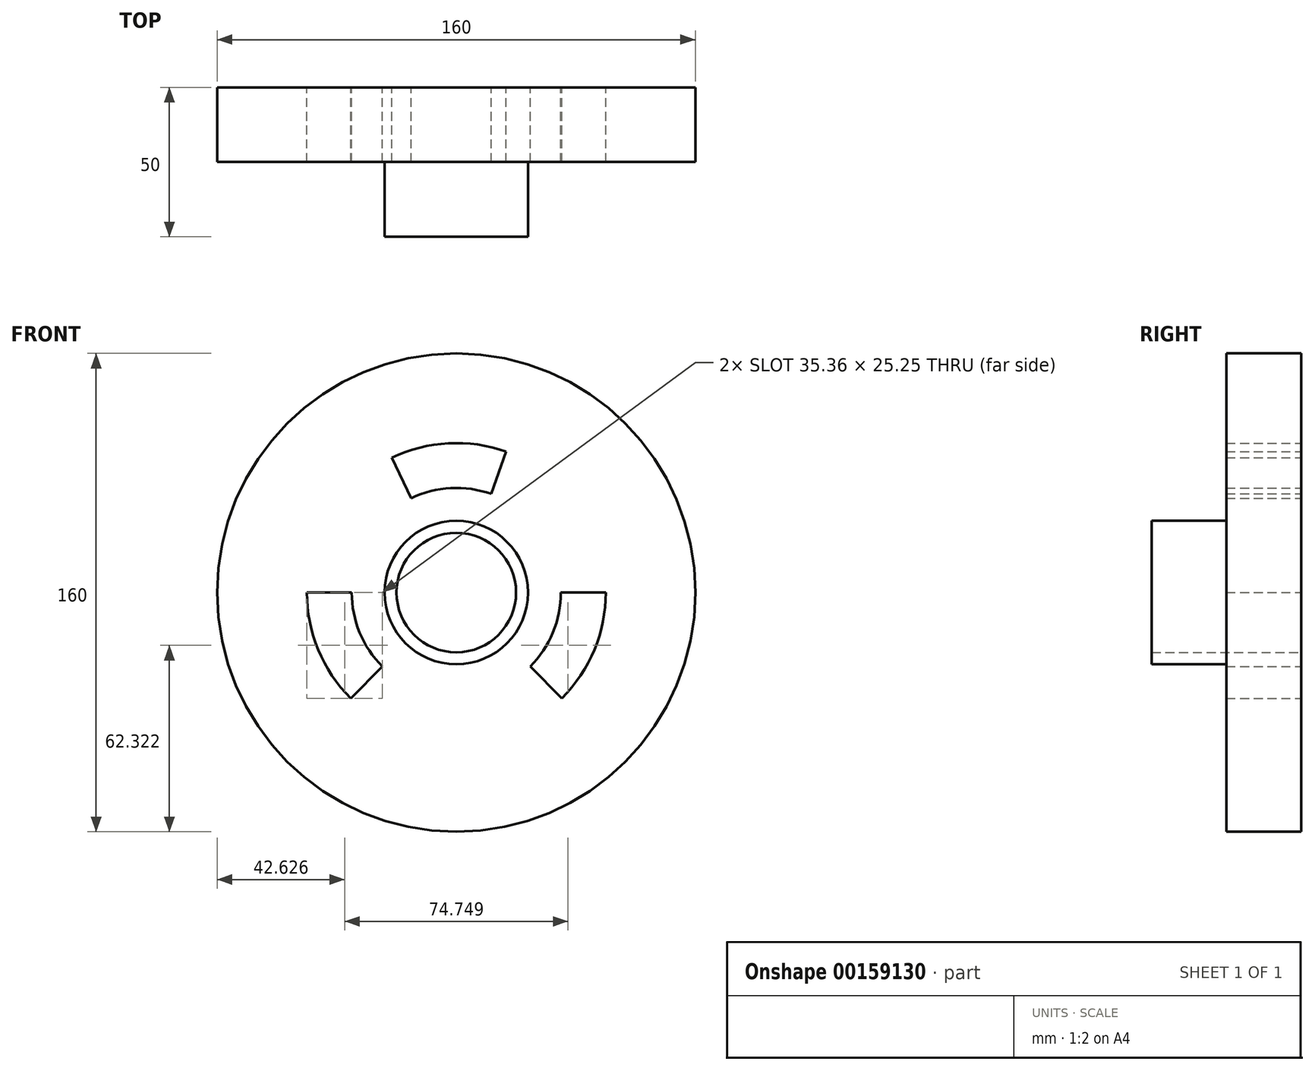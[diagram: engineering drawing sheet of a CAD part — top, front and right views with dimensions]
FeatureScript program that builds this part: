
annotation { "Feature Type Name" : "Feature", "Feature Type Description" : "" }
export const myFeature = defineFeature(function(context is Context, id is Id, definition is map)
    precondition{}
    {
        {
            var Q0;
            Q0=qCreatedBy(makeId("Front.planeOp"),FACE);
            var sketch = newSketch(context, id + "F0", { "sketchPlane" : qUnion([Q0])});
            skCircle(sketch, "E0", {"center": v(0, 0) * mm, "radius": 50 * mm});
            skCircle(sketch, "E1", {"center": v(0, 0) * mm, "radius": 20 * mm});
            skCircle(sketch, "E2", {"center": v(0, 0) * mm, "radius": 80 * mm});
            skLineSegment(sketch, "E3", {"start": v(0, 0) * mm, "end": v(-38.3, 80.1) * mm});
            skLineSegment(sketch, "E4", {"start": v(0, 0) * mm, "end": v(29.56, 83.72) * mm});
            skCircle(sketch, "E5", {"center": v(0, 0) * mm, "radius": 35 * mm});
            skCircle(sketch, "E6", {"center": v(0, 0) * mm, "radius": 24 * mm});
            skLineSegment(sketch, "E7", {"start": v(83.36, 161.24) * mm, "end": v(111.84, 161.24) * mm});
            skArc(sketch, "E8", {"start": v(83.36, 176.24) * mm, "mid": v(68.36, 161.24) * mm, "end": v(83.36, 146.24) * mm});
            skPoint(sketch, "E9", {"position": v(-21.57, 45.1) * mm});
            skPoint(sketch, "E10", {"position": v(-15.1, 31.58) * mm});
            skPoint(sketch, "E11", {"position": v(16.65, 47.15) * mm});
            skPoint(sketch, "E12", {"position": v(11.65, 33) * mm});
            skLineSegment(sketch, "E13", {"start": v(0, 0) * mm, "end": v(109.13, 0) * mm});
            skLineSegment(sketch, "E14", {"start": v(0, 0) * mm, "end": v(-88.87, 0) * mm});
            skLineSegment(sketch, "E15", {"start": v(0, 0) * mm, "end": v(-75.12, -75.12) * mm});
            skLineSegment(sketch, "E16", {"start": v(0, 0) * mm, "end": v(67.75, -67.75) * mm});
            skPoint(sketch, "E17", {"position": v(-50, 0) * mm});
            skPoint(sketch, "E18", {"position": v(-35.36, -35.36) * mm});
            skPoint(sketch, "E19", {"position": v(35.36, -35.36) * mm});
            skPoint(sketch, "E20", {"position": v(50, 0) * mm});
            skSolve(sketch);
        }
        {
            var Q0;
            Q0 = qSketchRegion(id + "F0", true);
            var Q1;
            {var subQ0=sQuery(id+"F0.wireOp",EDGE,"E4");var subQ1=sQuery(id+"F0.wireOp",EDGE,"E0");var subQ2=makeQuery(id+"F0.imprint","INTERSECT",VERTEX,{"derivedFrom":[subQ1,subQ0]});Q1=makeQuery(id+"F0.imprint","IMPRINT",FACE,{"disambiguationData":[TD([[makeQuery(id+"F0.imprint","IMPRINT",EDGE,{"disambiguationData":[TD([[subQ2,1.0]])],"derivedFrom":subQ1}),1.0]])]});}
            var Q2;
            {var subQ0=sQuery(id+"F0.wireOp",EDGE,"E3");var subQ1=sQuery(id+"F0.wireOp",EDGE,"E0");var subQ2=makeQuery(id+"F0.imprint","INTERSECT",VERTEX,{"derivedFrom":[subQ1,subQ0]});Q2=makeQuery(id+"F0.imprint","IMPRINT",FACE,{"disambiguationData":[TD([[makeQuery(id+"F0.imprint","IMPRINT",EDGE,{"disambiguationData":[TD([[subQ2,-1.0]])],"derivedFrom":subQ1}),1.0]])]});}
            var Q3;
            {var subQ0=sQuery(id+"F0.wireOp",EDGE,"E15");var subQ1=sQuery(id+"F0.wireOp",EDGE,"E0");var subQ2=makeQuery(id+"F0.imprint","INTERSECT",VERTEX,{"derivedFrom":[subQ1,subQ0]});Q3=makeQuery(id+"F0.imprint","IMPRINT",FACE,{"disambiguationData":[TD([[makeQuery(id+"F0.imprint","IMPRINT",EDGE,{"disambiguationData":[TD([[subQ2,-1.0]])],"derivedFrom":subQ1}),1.0]])]});}
            var Q4;
            {var subQ0=sQuery(id+"F0.wireOp",EDGE,"E6");var subQ1=sQuery(id+"F0.wireOp",EDGE,"E3");var subQ2=makeQuery(id+"F0.imprint","INTERSECT",VERTEX,{"derivedFrom":[subQ1,subQ0]});Q4=makeQuery(id+"F0.imprint","IMPRINT",FACE,{"disambiguationData":[TD([[makeQuery(id+"F0.imprint","IMPRINT",EDGE,{"disambiguationData":[TD([[subQ2,-1.0]])],"derivedFrom":subQ1}),1.0]])]});}
            var Q5;
            {var subQ0=sQuery(id+"F0.wireOp",EDGE,"E6");var subQ1=sQuery(id+"F0.wireOp",EDGE,"E3");var subQ2=makeQuery(id+"F0.imprint","INTERSECT",VERTEX,{"derivedFrom":[subQ1,subQ0]});Q5=makeQuery(id+"F0.imprint","IMPRINT",FACE,{"disambiguationData":[TD([[makeQuery(id+"F0.imprint","IMPRINT",EDGE,{"disambiguationData":[TD([[subQ2,-1.0]])],"derivedFrom":subQ1}),-1.0]])]});}
            var Q6;
            {var subQ0=sQuery(id+"F0.wireOp",EDGE,"E6");var subQ1=sQuery(id+"F0.wireOp",EDGE,"E4");var subQ2=makeQuery(id+"F0.imprint","INTERSECT",VERTEX,{"derivedFrom":[subQ1,subQ0]});Q6=makeQuery(id+"F0.imprint","IMPRINT",FACE,{"disambiguationData":[TD([[makeQuery(id+"F0.imprint","IMPRINT",EDGE,{"disambiguationData":[TD([[subQ2,-1.0]])],"derivedFrom":subQ1}),-1.0]])]});}
            var Q7;
            {var subQ0=sQuery(id+"F0.wireOp",EDGE,"E13");var subQ1=sQuery(id+"F0.wireOp",EDGE,"E5");var subQ2=makeQuery(id+"F0.imprint","INTERSECT",VERTEX,{"derivedFrom":[subQ1,subQ0]});Q7=makeQuery(id+"F0.imprint","IMPRINT",FACE,{"disambiguationData":[TD([[makeQuery(id+"F0.imprint","IMPRINT",EDGE,{"disambiguationData":[TD([[subQ2,1.0]])],"derivedFrom":subQ1}),1.0]])]});}
            var Q8;
            {var subQ0=sQuery(id+"F0.wireOp",EDGE,"E15");var subQ1=sQuery(id+"F0.wireOp",EDGE,"E5");var subQ2=makeQuery(id+"F0.imprint","INTERSECT",VERTEX,{"derivedFrom":[subQ1,subQ0]});Q8=makeQuery(id+"F0.imprint","IMPRINT",FACE,{"disambiguationData":[TD([[makeQuery(id+"F0.imprint","IMPRINT",EDGE,{"disambiguationData":[TD([[subQ2,-1.0]])],"derivedFrom":subQ1}),1.0]])]});}
            var Q9;
            {var subQ0=sQuery(id+"F0.wireOp",EDGE,"E14");var subQ1=sQuery(id+"F0.wireOp",EDGE,"E5");var subQ2=makeQuery(id+"F0.imprint","INTERSECT",VERTEX,{"derivedFrom":[subQ1,subQ0]});Q9=makeQuery(id+"F0.imprint","IMPRINT",FACE,{"disambiguationData":[TD([[makeQuery(id+"F0.imprint","IMPRINT",EDGE,{"disambiguationData":[TD([[subQ2,-1.0]])],"derivedFrom":subQ1}),1.0]])]});}
            extrude(context, id + "F1", {"entities" : qUnion([Q0, Q1, Q2, Q3, Q4, Q5, Q6, Q7, Q8, Q9]), "depth" : 25 * mm});
        }
        {
            var Q0;
            Q0=qCreatedBy(makeId("Front.planeOp"),FACE);
            var sketch = newSketch(context, id + "F2", { "sketchPlane" : qUnion([Q0])});
            skCircle(sketch, "E21", {"center": v(0, 0) * mm, "radius": 24 * mm});
            skCircle(sketch, "E22", {"center": v(0, 0) * mm, "radius": 20 * mm});
            skSolve(sketch);
        }
        {
            var Q0;
            Q0=makeQuery(id+"F2.imprint","IMPRINT",FACE,{"disambiguationData":[TD([[makeQuery(id+"F2.imprint","IMPRINT",EDGE,{"derivedFrom":sQuery(id+"F2.wireOp",EDGE,"E21")}),1.0]])]});
            extrude(context, id + "F3", {"entities" : qUnion([Q0]), "operationType" : NewBodyOperationType.ADD, "depth" : 50 * mm});
        }
    });
